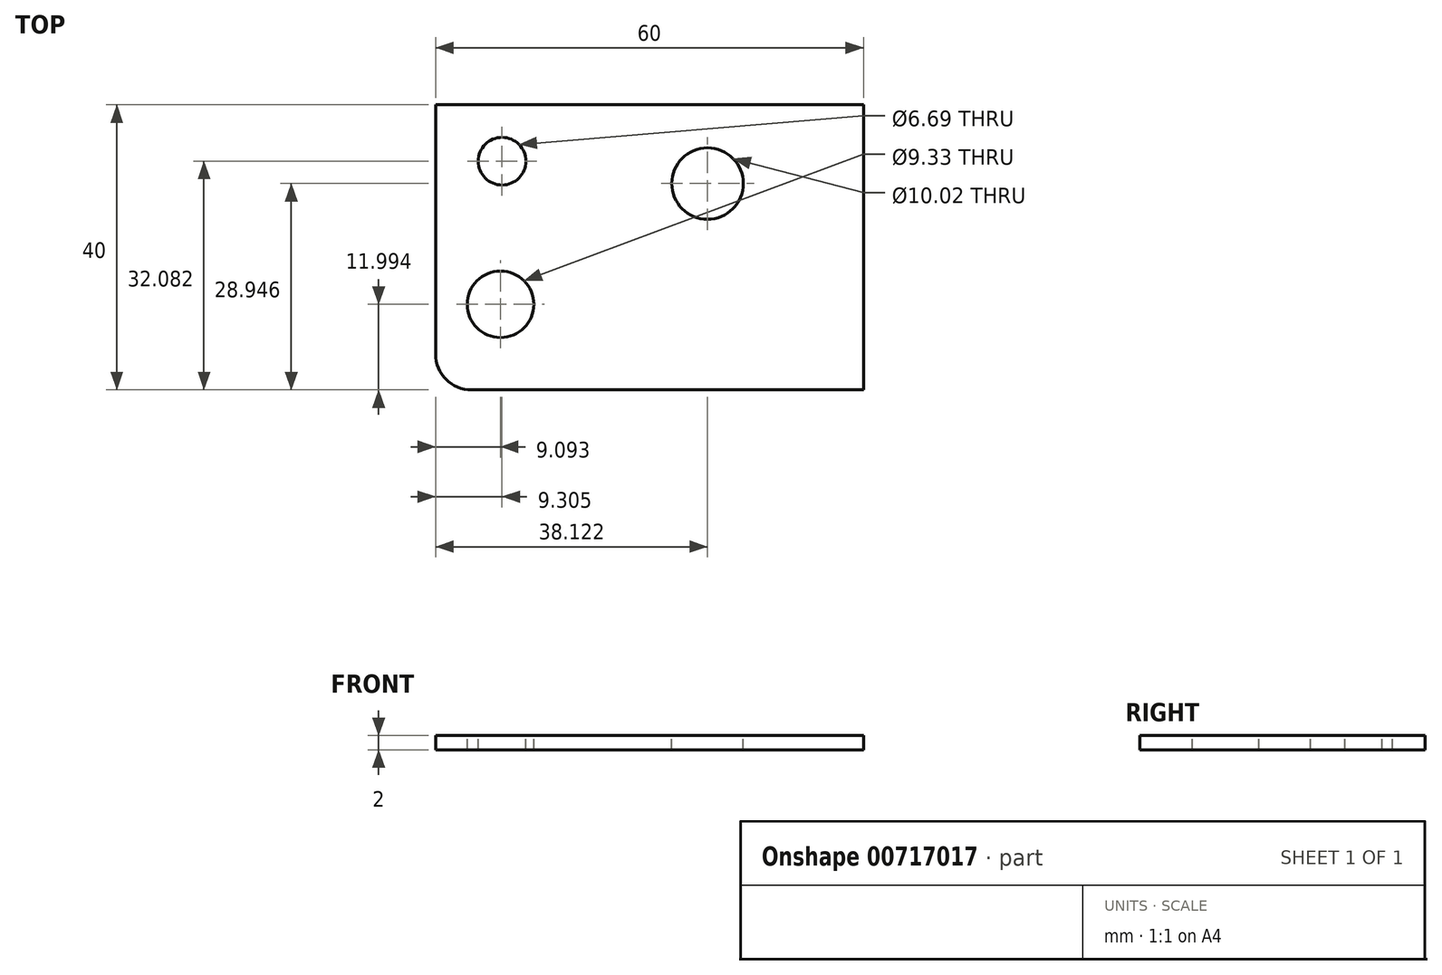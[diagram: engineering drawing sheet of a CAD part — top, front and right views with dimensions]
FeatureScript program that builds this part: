
annotation { "Feature Type Name" : "Feature", "Feature Type Description" : "" }
export const myFeature = defineFeature(function(context is Context, id is Id, definition is map)
    precondition{}
    {
        {
            var Q0;
            Q0=qCreatedBy(makeId("Top.planeOp"),FACE);
            var sketch = newSketch(context, id + "F0", { "sketchPlane" : qUnion([Q0])});
            skLineSegment(sketch, "E0.bottom", {"start": v(-27.36, 18.9) * mm, "end": v(32.64, 18.9) * mm});
            skLineSegment(sketch, "E0.top", {"start": v(-27.36, -21.1) * mm, "end": v(32.64, -21.1) * mm});
            skLineSegment(sketch, "E0.left", {"start": v(-27.36, 18.9) * mm, "end": v(-27.36, -21.1) * mm});
            skLineSegment(sketch, "E0.right", {"start": v(32.64, 18.9) * mm, "end": v(32.64, -21.1) * mm});
            skSolve(sketch);
        }
        {
            var Q0;
            Q0 = qSketchRegion(id + "F0", true);
            extrude(context, id + "F1", {"entities" : qUnion([Q0]), "depth" : 2 * mm, "offsetDistance" : 25 * mm});
        }
        {
            var Q0;
            Q0=makeQuery(id+"F1.opExtrude","CAP_FACE",FACE,{"disambiguationData":[OSD([sQuery(id+"F0.wireOp",EDGE,"E0.bottom"),sQuery(id+"F0.wireOp",EDGE,"E0.top"),sQuery(id+"F0.wireOp",EDGE,"E0.left"),sQuery(id+"F0.wireOp",EDGE,"E0.right")])],"isStart":false});
            var sketch = newSketch(context, id + "F2", { "sketchPlane" : qUnion([Q0])});
            skCircle(sketch, "E1", {"center": v(-18.05, 10.97) * mm, "radius": 3.34 * mm});
            skCircle(sketch, "E2", {"center": v(-18.27, -9.12) * mm, "radius": 4.66 * mm});
            skCircle(sketch, "E3", {"center": v(10.76, 7.84) * mm, "radius": 5.01 * mm});
            skSolve(sketch);
        }
        {
            var Q0;
            Q0 = qSketchRegion(id + "F2", true);
            extrude(context, id + "F3", {"entities" : qUnion([Q0]), "operationType" : NewBodyOperationType.REMOVE, "oppositeDirection" : true, "depth" : 2 * mm, "offsetDistance" : 25 * mm});
        }
        {
            var Q0;
            Q0=makeQuery(id+"F1.opExtrude","SWEPT_EDGE",EDGE,{"disambiguationData":[OSD([sQuery(id+"F0.wireOp",EDGE,"E0.top"),sQuery(id+"F0.wireOp",EDGE,"E0.left")])]});
            fillet(context, id + "F4", {"entities" : qUnion([Q0]), "radius" : 5 * mm, "tangentPropagation" : true, "allowEdgeOverflow" : false});
        }
    });
